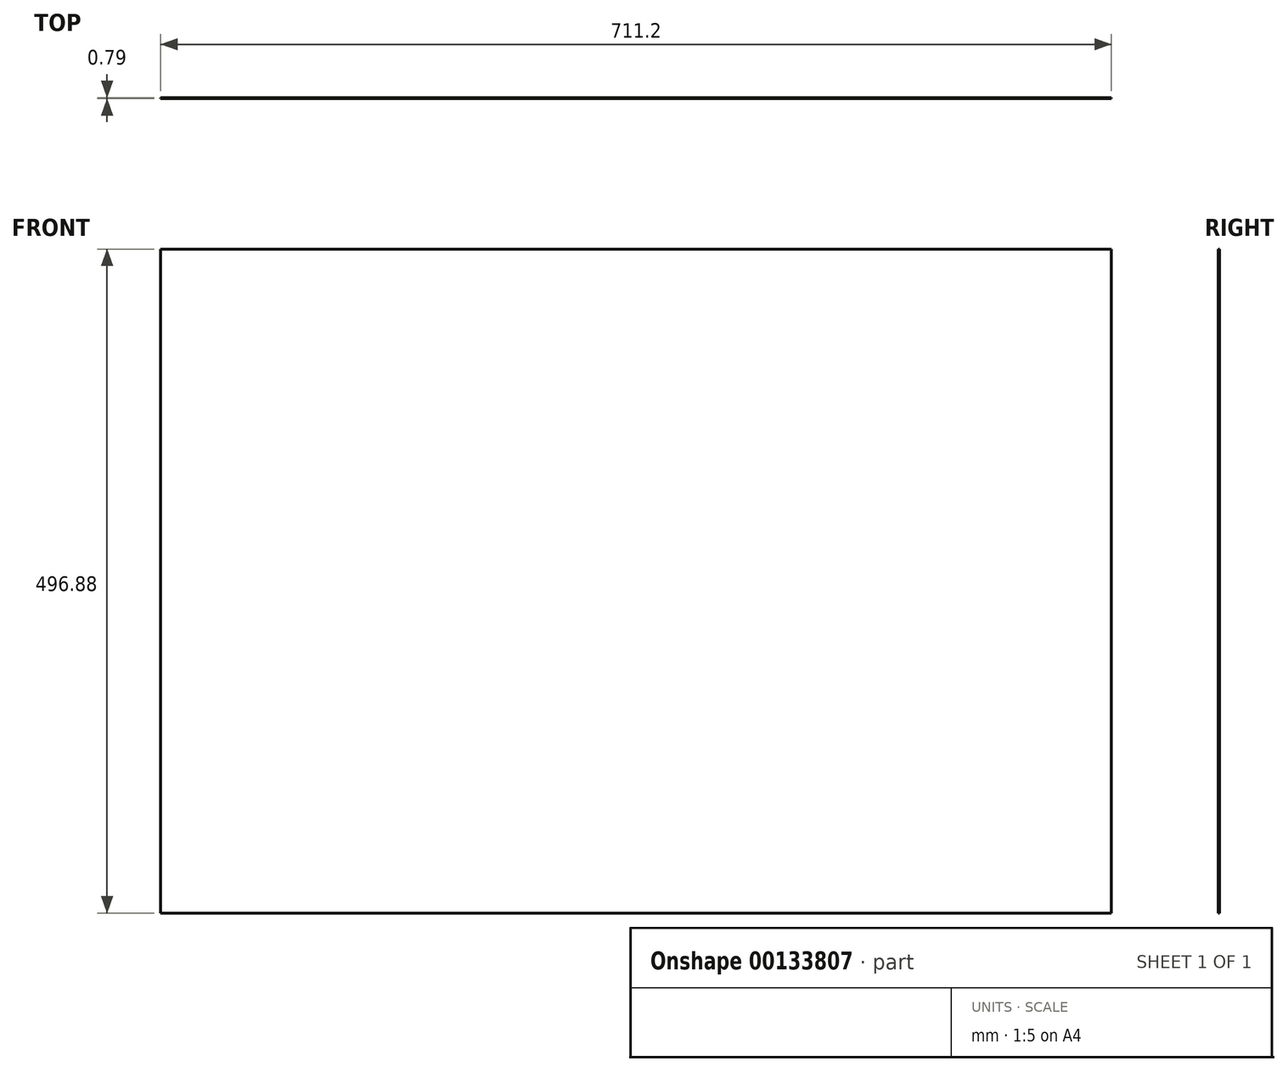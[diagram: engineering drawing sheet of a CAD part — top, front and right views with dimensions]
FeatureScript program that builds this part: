
annotation { "Feature Type Name" : "Feature", "Feature Type Description" : "" }
export const myFeature = defineFeature(function(context is Context, id is Id, definition is map)
    precondition{}
    {
        {
            var Q0;
            Q0=qCreatedBy(makeId("Front.planeOp"),FACE);
            var sketch = newSketch(context, id + "F0", { "sketchPlane" : qUnion([Q0])});
            skLineSegment(sketch, "E0.bottom", {"start": v(355.6, -248.44) * mm, "end": v(-355.6, -248.44) * mm});
            skLineSegment(sketch, "E0.top", {"start": v(355.6, 248.44) * mm, "end": v(-355.6, 248.44) * mm});
            skLineSegment(sketch, "E0.left", {"start": v(355.6, -248.44) * mm, "end": v(355.6, 248.44) * mm});
            skLineSegment(sketch, "E0.right", {"start": v(-355.6, -248.44) * mm, "end": v(-355.6, 248.44) * mm});
            skPoint(sketch, "E0.middle", {"position": v(0, 0) * mm});
            skSolve(sketch);
        }
        {
            var Q0;
            Q0 = qSketchRegion(id + "F0", true);
            extrude(context, id + "F1", {"entities" : qUnion([Q0]), "depth" : 0.8 * mm});
        }
    });
